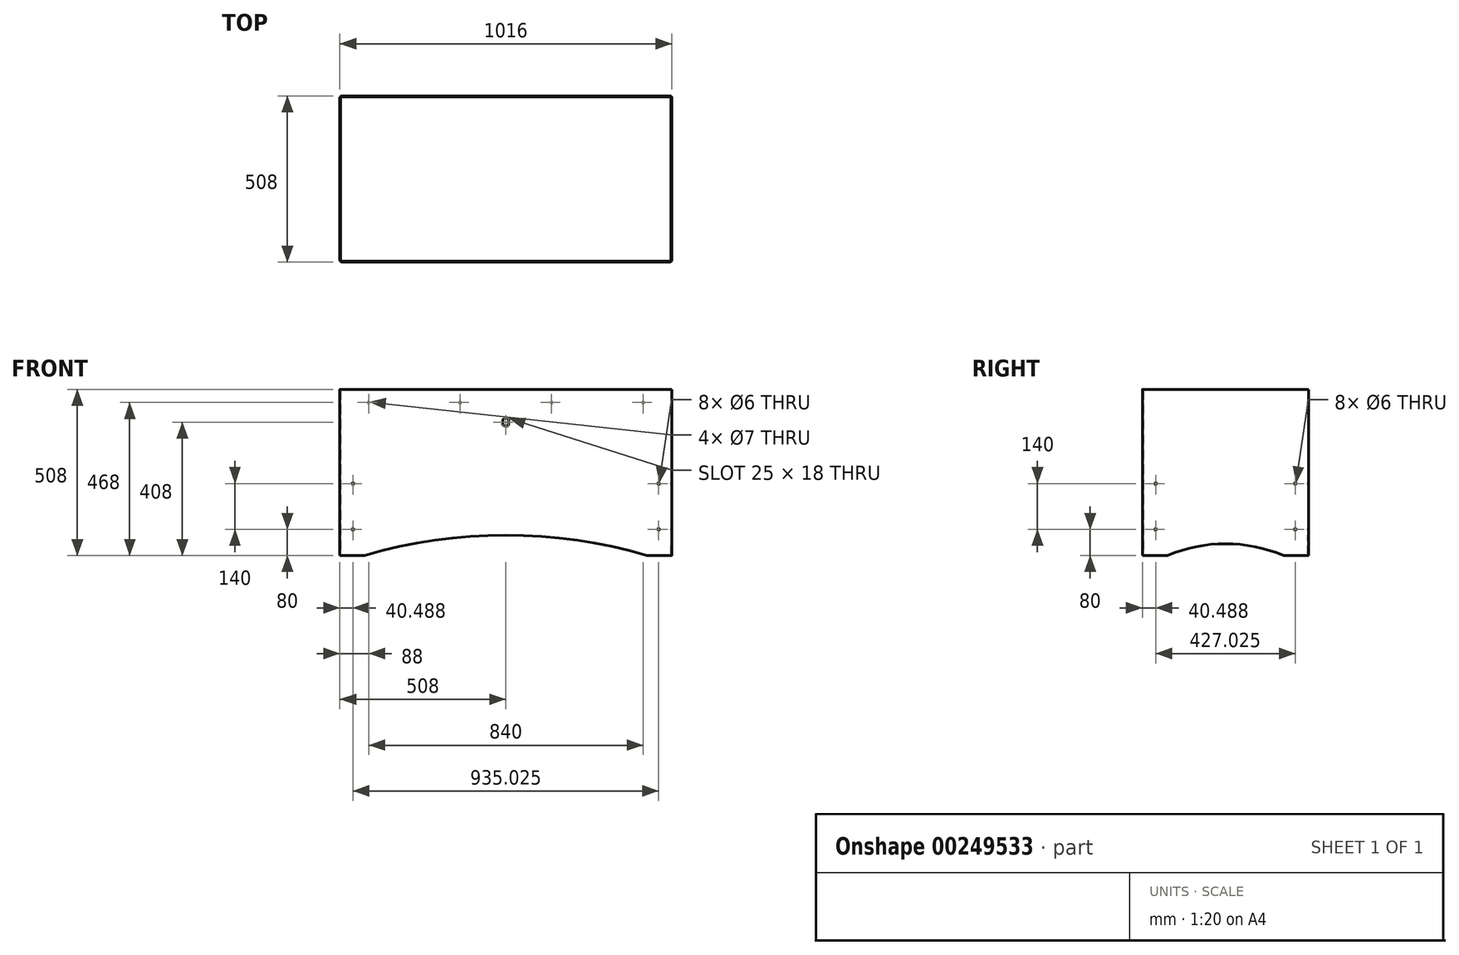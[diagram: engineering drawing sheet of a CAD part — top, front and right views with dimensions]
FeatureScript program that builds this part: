
annotation { "Feature Type Name" : "Feature", "Feature Type Description" : "" }
export const myFeature = defineFeature(function(context is Context, id is Id, definition is map)
    precondition{}
    {
        {
            var Q0;
            Q0=qCreatedBy(makeId("Top.planeOp"),FACE);
            var sketch = newSketch(context, id + "F0", { "sketchPlane" : qUnion([Q0])});
            skLineSegment(sketch, "E0.bottom", {"start": v(501.65, 254) * mm, "end": v(-501.65, 254) * mm});
            skLineSegment(sketch, "E0.top", {"start": v(501.65, -254) * mm, "end": v(-501.65, -254) * mm});
            skLineSegment(sketch, "E0.left", {"start": v(508, 247.65) * mm, "end": v(508, -247.65) * mm});
            skLineSegment(sketch, "E0.right", {"start": v(-508, 247.65) * mm, "end": v(-508, -247.65) * mm});
            skPoint(sketch, "E0.middle", {"position": v(0, 0) * mm});
            skPoint(sketch, "E1.visualSharp", {"position": v(-508, 254) * mm});
            skArc(sketch, "E1.filletArc", {"start": v(-501.65, 254) * mm, "mid": v(-506.14, 252.14) * mm, "end": v(-508, 247.65) * mm});
            skPoint(sketch, "E2.visualSharp", {"position": v(508, 254) * mm});
            skArc(sketch, "E2.filletArc", {"start": v(508, 247.65) * mm, "mid": v(506.14, 252.14) * mm, "end": v(501.65, 254) * mm});
            skPoint(sketch, "E3.visualSharp", {"position": v(508, -254) * mm});
            skArc(sketch, "E3.filletArc", {"start": v(501.65, -254) * mm, "mid": v(506.14, -252.14) * mm, "end": v(508, -247.65) * mm});
            skPoint(sketch, "E4.visualSharp", {"position": v(-508, -254) * mm});
            skArc(sketch, "E4.filletArc", {"start": v(-508, -247.65) * mm, "mid": v(-506.14, -252.14) * mm, "end": v(-501.65, -254) * mm});
            skSolve(sketch);
        }
        {
            var Q0;
            Q0 = qSketchRegion(id + "F0", true);
            extrude(context, id + "F1", {"entities" : qUnion([Q0]), "depth" : 508 * mm});
        }
        {
            var Q0;
            Q0=makeQuery(id+"F1.opExtrude","CAP_FACE",FACE,{"disambiguationData":[OSD([sQuery(id+"F0.wireOp",EDGE,"E0.bottom"),sQuery(id+"F0.wireOp",EDGE,"E0.top"),sQuery(id+"F0.wireOp",EDGE,"E0.left"),sQuery(id+"F0.wireOp",EDGE,"E0.right"),sQuery(id+"F0.wireOp",EDGE,"E1.filletArc"),sQuery(id+"F0.wireOp",EDGE,"E2.filletArc"),sQuery(id+"F0.wireOp",EDGE,"E3.filletArc"),sQuery(id+"F0.wireOp",EDGE,"E4.filletArc")])],"isStart":false});
            var Q1;
            Q1=makeQuery(id+"F1.opExtrude","CAP_FACE",FACE,{"disambiguationData":[OSD([sQuery(id+"F0.wireOp",EDGE,"E0.bottom"),sQuery(id+"F0.wireOp",EDGE,"E0.top"),sQuery(id+"F0.wireOp",EDGE,"E0.left"),sQuery(id+"F0.wireOp",EDGE,"E0.right"),sQuery(id+"F0.wireOp",EDGE,"E1.filletArc"),sQuery(id+"F0.wireOp",EDGE,"E2.filletArc"),sQuery(id+"F0.wireOp",EDGE,"E3.filletArc"),sQuery(id+"F0.wireOp",EDGE,"E4.filletArc")])],"isStart":true});
            shell(context, id + "F2", {"entities" : qUnion([Q0, Q1]), "thickness" : 2.54 * mm});
        }
        {
            var Q0;
            Q0=qCreatedBy(makeId("Front.planeOp"),FACE);
            var sketch = newSketch(context, id + "F3", { "sketchPlane" : qUnion([Q0])});
            skLineSegment(sketch, "E5", {"start": v(0, 0) * mm, "end": v(0, -1461.55) * mm, "construction": true});
            skArc(sketch, "E6", {"start": v(-431.8, 0) * mm, "mid": v(0, 62.45) * mm, "end": v(431.8, 0) * mm});
            skLineSegment(sketch, "E7", {"start": v(-431.8, 0) * mm, "end": v(431.8, 0) * mm});
            skSolve(sketch);
        }
        {
            var Q0;
            Q0 = qSketchRegion(id + "F3", true);
            extrude(context, id + "F4", {"entities" : qUnion([Q0]), "operationType" : NewBodyOperationType.REMOVE, "endBound" : BoundingType.SYMMETRIC, "oppositeDirection" : true, "depth" : 762 * mm});
        }
        {
            var Q0;
            Q0=qCreatedBy(makeId("Right.planeOp"),FACE);
            var sketch = newSketch(context, id + "F5", { "sketchPlane" : qUnion([Q0])});
            skLineSegment(sketch, "E8", {"start": v(0, 0) * mm, "end": v(0, -421.21) * mm, "construction": true});
            skArc(sketch, "E9", {"start": v(177.8, 0) * mm, "mid": v(0, 35.99) * mm, "end": v(-177.8, 0) * mm});
            skLineSegment(sketch, "E10", {"start": v(177.8, 0) * mm, "end": v(-177.8, 0) * mm});
            skSolve(sketch);
        }
        {
            var Q0;
            Q0 = qSketchRegion(id + "F5", true);
            extrude(context, id + "F6", {"entities" : qUnion([Q0]), "operationType" : NewBodyOperationType.REMOVE, "endBound" : BoundingType.SYMMETRIC, "oppositeDirection" : true, "depth" : 1270 * mm});
        }
        {
            var Q0;
            Q0=qCreatedBy(makeId("Front.planeOp"),FACE);
            var sketch = newSketch(context, id + "F7", { "sketchPlane" : qUnion([Q0])});
            skLineSegment(sketch, "E11", {"start": v(420, 468) * mm, "end": v(-420, 468) * mm, "construction": true});
            skLineSegment(sketch, "E12", {"start": v(0, 559.15) * mm, "end": v(0, 468) * mm, "construction": true});
            skPoint(sketch, "E12.startSnap0", {"position": v(0, 468) * mm});
            skPoint(sketch, "E12.endSnap0", {"position": v(0, 468) * mm});
            skCircle(sketch, "E13", {"center": v(420, 468) * mm, "radius": 3.5 * mm});
            skCircle(sketch, "E14", {"center": v(140, 468) * mm, "radius": 3.5 * mm});
            skCircle(sketch, "E15", {"center": v(-140, 468) * mm, "radius": 3.5 * mm});
            skCircle(sketch, "E16", {"center": v(-420, 468) * mm, "radius": 3.5 * mm});
            skSolve(sketch);
        }
        {
            var Q0;
            Q0 = qSketchRegion(id + "F7", true);
            extrude(context, id + "F8", {"entities" : qUnion([Q0]), "operationType" : NewBodyOperationType.REMOVE, "endBound" : BoundingType.THROUGH_ALL, "oppositeDirection" : true, "depth" : 25.4 * mm});
        }
        {
            var Q0;
            Q0=qCreatedBy(makeId("Front.planeOp"),FACE);
            var sketch = newSketch(context, id + "F9", { "sketchPlane" : qUnion([Q0])});
            skLineSegment(sketch, "E17", {"start": v(0, 508) * mm, "end": v(0, 408) * mm, "construction": true});
            skArc(sketch, "E18", {"start": v(-9, 399.33) * mm, "mid": v(0, 395.5) * mm, "end": v(9, 399.33) * mm});
            skLineSegment(sketch, "E19", {"start": v(-9, 416.67) * mm, "end": v(-9, 399.33) * mm});
            skLineSegment(sketch, "E20", {"start": v(9, 416.67) * mm, "end": v(9, 399.33) * mm});
            skArc(sketch, "E21.trimOffspring", {"start": v(9, 416.67) * mm, "mid": v(0, 420.5) * mm, "end": v(-9, 416.67) * mm});
            skSolve(sketch);
        }
        {
            var Q0;
            Q0 = qSketchRegion(id + "F9", true);
            extrude(context, id + "F10", {"entities" : qUnion([Q0]), "operationType" : NewBodyOperationType.REMOVE, "endBound" : BoundingType.THROUGH_ALL, "depth" : 25.4 * mm});
        }
        {
            var Q0;
            Q0=qCreatedBy(makeId("Front.planeOp"),FACE);
            var sketch = newSketch(context, id + "F11", { "sketchPlane" : qUnion([Q0])});
            skCircle(sketch, "E22", {"center": v(-467.51, 220) * mm, "radius": 3 * mm});
            skCircle(sketch, "E23", {"center": v(-467.51, 80) * mm, "radius": 3 * mm});
            skCircle(sketch, "E24", {"center": v(467.51, 220) * mm, "radius": 3 * mm});
            skCircle(sketch, "E25", {"center": v(467.51, 80) * mm, "radius": 3 * mm});
            skSolve(sketch);
        }
        {
            var Q0;
            Q0 = qSketchRegion(id + "F11", true);
            extrude(context, id + "F12", {"entities" : qUnion([Q0]), "operationType" : NewBodyOperationType.REMOVE, "endBound" : BoundingType.SYMMETRIC, "oppositeDirection" : true, "depth" : 762 * mm});
        }
        {
            var Q0;
            Q0=qCreatedBy(makeId("Right.planeOp"),FACE);
            var sketch = newSketch(context, id + "F13", { "sketchPlane" : qUnion([Q0])});
            skCircle(sketch, "E26", {"center": v(213.51, 220) * mm, "radius": 3 * mm});
            skCircle(sketch, "E27", {"center": v(213.51, 80) * mm, "radius": 3 * mm});
            skCircle(sketch, "E28", {"center": v(-213.51, 220) * mm, "radius": 3 * mm});
            skCircle(sketch, "E29", {"center": v(-213.51, 80) * mm, "radius": 3 * mm});
            skSolve(sketch);
        }
        {
            var Q0;
            Q0 = qSketchRegion(id + "F13", true);
            extrude(context, id + "F14", {"entities" : qUnion([Q0]), "operationType" : NewBodyOperationType.REMOVE, "endBound" : BoundingType.SYMMETRIC, "oppositeDirection" : true, "depth" : 2540 * mm});
        }
    });
